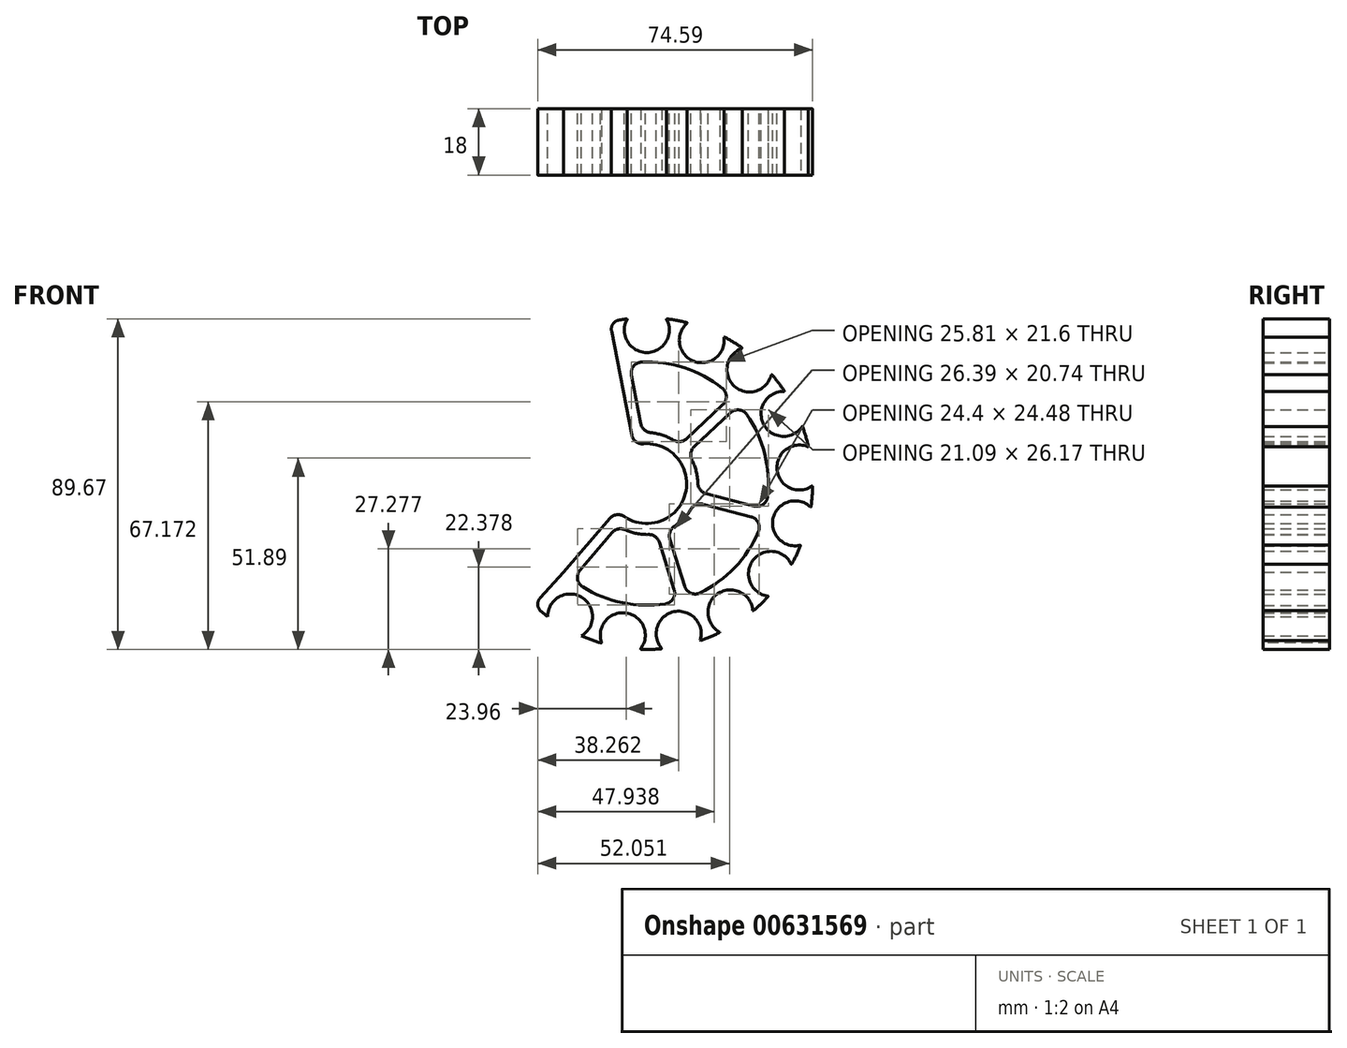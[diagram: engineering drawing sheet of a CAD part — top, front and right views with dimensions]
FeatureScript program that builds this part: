
annotation { "Feature Type Name" : "Feature", "Feature Type Description" : "" }
export const myFeature = defineFeature(function(context is Context, id is Id, definition is map)
    precondition{}
    {
        {
            var Q0;
            Q0=qCreatedBy(makeId("Front.planeOp"),FACE);
            var sketch = newSketch(context, id + "F0", { "sketchPlane" : qUnion([Q0])});
            skArc(sketch, "E0", {"start": v(-8.1, -7.18) * mm, "mid": v(10.47, -2.76) * mm, "end": v(-3.52, 10.24) * mm});
            skArc(sketch, "E1", {"start": v(-30.67, -32.93) * mm, "mid": v(43.46, -11.67) * mm, "end": v(-10.06, 43.86) * mm});
            skCircle(sketch, "E2", {"center": v(0, 41.65) * mm, "radius": 6.1 * mm});
            skCircle(sketch, "E3.1.0", {"center": v(14.93, 38.88) * mm, "radius": 6.1 * mm});
            skCircle(sketch, "E3.2.0", {"center": v(27.87, 30.95) * mm, "radius": 6.1 * mm});
            skCircle(sketch, "E3.3.0", {"center": v(37.11, 18.9) * mm, "radius": 6.1 * mm});
            skCircle(sketch, "E3.4.0", {"center": v(41.42, 4.35) * mm, "radius": 6.1 * mm});
            skCircle(sketch, "E3.5.0", {"center": v(40.23, -10.78) * mm, "radius": 6.1 * mm});
            skCircle(sketch, "E3.6.0", {"center": v(33.7, -24.48) * mm, "radius": 6.1 * mm});
            skCircle(sketch, "E3.7.0", {"center": v(22.68, -34.93) * mm, "radius": 6.1 * mm});
            skCircle(sketch, "E3.8.0", {"center": v(8.66, -40.74) * mm, "radius": 6.1 * mm});
            skCircle(sketch, "E3.9.0", {"center": v(-6.52, -41.14) * mm, "radius": 6.1 * mm});
            skLineSegment(sketch, "E3.anchor1", {"start": v(0, 0) * mm, "end": v(0, 41.65) * mm, "construction": true});
            skLineSegment(sketch, "E3.anchor2", {"start": v(0, 0) * mm, "end": v(-20.83, -36.07) * mm, "construction": true});
            skLineSegment(sketch, "E4", {"start": v(0, 0) * mm, "end": v(-8.59, 44.17) * mm, "construction": true});
            skLineSegment(sketch, "E5", {"start": v(0, 0) * mm, "end": v(-30.47, -33.11) * mm, "construction": true});
            skArc(sketch, "E6.0", {"start": v(-22.55, -24.1) * mm, "mid": v(31.91, -8.4) * mm, "end": v(-7.76, 32.07) * mm});
            skLineSegment(sketch, "E7.0", {"start": v(-0.57, 10.8) * mm, "end": v(-4.82, 32.65) * mm});
            skLineSegment(sketch, "E8.0", {"start": v(-3.52, 10.24) * mm, "end": v(-7.76, 32.07) * mm});
            skLineSegment(sketch, "E9.trimOffspring", {"start": v(-10.06, 43.86) * mm, "end": v(-10.06, 43.89) * mm});
            skLineSegment(sketch, "E10.trimOffspring", {"start": v(-7.11, 44.43) * mm, "end": v(-7.12, 44.46) * mm});
            skLineSegment(sketch, "E11.1.0", {"start": v(6.8, 8.42) * mm, "end": v(23.03, 23.63) * mm});
            skLineSegment(sketch, "E11.1.1", {"start": v(8.85, 6.23) * mm, "end": v(25.08, 21.44) * mm});
            skLineSegment(sketch, "E11.2.0", {"start": v(10.75, -1.28) * mm, "end": v(32.26, -6.94) * mm});
            skLineSegment(sketch, "E11.2.1", {"start": v(9.99, -4.18) * mm, "end": v(31.5, -9.84) * mm});
            skLineSegment(sketch, "E11.3.0", {"start": v(4.63, -9.78) * mm, "end": v(11.28, -31.01) * mm});
            skLineSegment(sketch, "E11.3.1", {"start": v(1.77, -10.68) * mm, "end": v(8.42, -31.9) * mm});
            skLineSegment(sketch, "E11.4.0", {"start": v(-5.82, -9.13) * mm, "end": v(-20.27, -26.04) * mm});
            skLineSegment(sketch, "E11.4.1", {"start": v(-8.1, -7.18) * mm, "end": v(-22.55, -24.1) * mm});
            skLineSegment(sketch, "E11.anchor1", {"start": v(0, 0) * mm, "end": v(-3.52, 10.24) * mm, "construction": true});
            skLineSegment(sketch, "E11.anchor2", {"start": v(0, 0) * mm, "end": v(-5.82, -9.13) * mm, "construction": true});
            skLineSegment(sketch, "E12", {"start": v(-10.06, 43.86) * mm, "end": v(-7.76, 32.07) * mm});
            skLineSegment(sketch, "E13", {"start": v(-22.55, -24.1) * mm, "end": v(-30.67, -32.93) * mm});
            skArc(sketch, "E14.0", {"start": v(-10.07, -9.48) * mm, "mid": v(13.37, -3.52) * mm, "end": v(-4.1, 13.2) * mm});
            skCircle(sketch, "E15.1.10.0", {"center": v(-20.83, -36.07) * mm, "radius": 6.1 * mm});
            skSolve(sketch);
        }
        {
            var Q0;
            {var subQ20=sQuery(id+"F0.wireOp",EDGE,"E0");var subQ25=sQuery(id+"F0.wireOp",EDGE,"E4");var subQ27=makeQuery(id+"F0.imprint","INTERSECT",VERTEX,{"derivedFrom":[subQ20,subQ25]});Q0=makeQuery(id+"F0.imprint","IMPRINT",FACE,{"disambiguationData":[TD([[makeQuery(id+"F0.imprint","IMPRINT",EDGE,{"disambiguationData":[TD([[subQ27,1.0]])],"derivedFrom":subQ20}),-1.0]])]});}
            var Q1;
            {var subQ1=sQuery(id+"F0.wireOp",EDGE,"E6.0");var subQ3=sQuery(id+"F0.wireOp",EDGE,"E7.0");var subQ4=makeQuery(id+"F0.imprint","INTERSECT",VERTEX,{"derivedFrom":[subQ1,subQ3]});Q1=makeQuery(id+"F0.imprint","IMPRINT",FACE,{"disambiguationData":[TD([[makeQuery(id+"F0.imprint","IMPRINT",EDGE,{"disambiguationData":[TD([[subQ4,1.0]])],"derivedFrom":subQ3}),1.0]])]});}
            var Q2;
            {var subQ0=sQuery(id+"F0.wireOp",EDGE,"E11.1.0");var subQ1=sQuery(id+"F0.wireOp",EDGE,"E6.0");var subQ2=makeQuery(id+"F0.imprint","INTERSECT",VERTEX,{"derivedFrom":[subQ1,subQ0]});Q2=makeQuery(id+"F0.imprint","IMPRINT",FACE,{"disambiguationData":[TD([[makeQuery(id+"F0.imprint","IMPRINT",EDGE,{"disambiguationData":[TD([[subQ2,1.0]])],"derivedFrom":subQ1}),1.0]])]});}
            var Q3;
            {var subQ0=sQuery(id+"F0.wireOp",EDGE,"E11.2.0");var subQ1=sQuery(id+"F0.wireOp",EDGE,"E6.0");var subQ2=makeQuery(id+"F0.imprint","INTERSECT",VERTEX,{"derivedFrom":[subQ1,subQ0]});Q3=makeQuery(id+"F0.imprint","IMPRINT",FACE,{"disambiguationData":[TD([[makeQuery(id+"F0.imprint","IMPRINT",EDGE,{"disambiguationData":[TD([[subQ2,1.0]])],"derivedFrom":subQ1}),1.0]])]});}
            var Q4;
            {var subQ0=sQuery(id+"F0.wireOp",EDGE,"E11.3.0");var subQ1=sQuery(id+"F0.wireOp",EDGE,"E6.0");var subQ2=makeQuery(id+"F0.imprint","INTERSECT",VERTEX,{"derivedFrom":[subQ1,subQ0]});Q4=makeQuery(id+"F0.imprint","IMPRINT",FACE,{"disambiguationData":[TD([[makeQuery(id+"F0.imprint","IMPRINT",EDGE,{"disambiguationData":[TD([[subQ2,1.0]])],"derivedFrom":subQ1}),1.0]])]});}
            var Q5;
            {var subQ1=sQuery(id+"F0.wireOp",EDGE,"E6.0");var subQ3=sQuery(id+"F0.wireOp",EDGE,"E11.4.0");var subQ4=makeQuery(id+"F0.imprint","INTERSECT",VERTEX,{"derivedFrom":[subQ1,subQ3]});Q5=makeQuery(id+"F0.imprint","IMPRINT",FACE,{"disambiguationData":[TD([[makeQuery(id+"F0.imprint","IMPRINT",EDGE,{"disambiguationData":[TD([[subQ4,1.0]])],"derivedFrom":subQ3}),-1.0]])]});}
            var Q6;
            {var subQ29=sQuery(id+"F0.wireOp",EDGE,"E12");Q6=makeQuery(id+"F0.imprint","IMPRINT",FACE,{"disambiguationData":[TD([[makeQuery(id+"F0.imprint","IMPRINT",EDGE,{"derivedFrom":subQ29}),1.0]])]});}
            extrude(context, id + "F1", {"entities" : qUnion([Q0, Q1, Q2, Q3, Q4, Q5, Q6]), "depth" : 18 * mm, "offsetDistance" : 25 * mm});
        }
        {
            var Q0;
            {var subQ0=sQuery(id+"F0.wireOp",EDGE,"E3.9.0");var subQ1=sQuery(id+"F0.wireOp",EDGE,"E1");Q0=makeQuery(id+"F1.opExtrude","SWEPT_EDGE",EDGE,{"disambiguationData":[OSD([subQ1,subQ0]),TDD([makeQuery(id+"F0.imprint","INTERSECT",VERTEX,{"disambiguationData":[OD(0.0)],"derivedFrom":[subQ1,subQ0]})])]});}
            var Q1;
            {var subQ0=sQuery(id+"F0.wireOp",EDGE,"E3.9.0");var subQ1=sQuery(id+"F0.wireOp",EDGE,"E1");Q1=makeQuery(id+"F1.opExtrude","SWEPT_EDGE",EDGE,{"disambiguationData":[OSD([subQ1,subQ0]),TDD([makeQuery(id+"F0.imprint","INTERSECT",VERTEX,{"disambiguationData":[OD(1.0)],"derivedFrom":[subQ1,subQ0]})])]});}
            var Q2;
            {var subQ0=sQuery(id+"F0.wireOp",EDGE,"E3.8.0");var subQ1=sQuery(id+"F0.wireOp",EDGE,"E1");Q2=makeQuery(id+"F1.opExtrude","SWEPT_EDGE",EDGE,{"disambiguationData":[OSD([subQ1,subQ0]),TDD([makeQuery(id+"F0.imprint","INTERSECT",VERTEX,{"disambiguationData":[OD(0.0)],"derivedFrom":[subQ1,subQ0]})])]});}
            var Q3;
            {var subQ0=sQuery(id+"F0.wireOp",EDGE,"E3.8.0");var subQ1=sQuery(id+"F0.wireOp",EDGE,"E1");Q3=makeQuery(id+"F1.opExtrude","SWEPT_EDGE",EDGE,{"disambiguationData":[OSD([subQ1,subQ0]),TDD([makeQuery(id+"F0.imprint","INTERSECT",VERTEX,{"disambiguationData":[OD(1.0)],"derivedFrom":[subQ1,subQ0]})])]});}
            var Q4;
            {var subQ0=sQuery(id+"F0.wireOp",EDGE,"E3.7.0");var subQ1=sQuery(id+"F0.wireOp",EDGE,"E1");Q4=makeQuery(id+"F1.opExtrude","SWEPT_EDGE",EDGE,{"disambiguationData":[OSD([subQ1,subQ0]),TDD([makeQuery(id+"F0.imprint","INTERSECT",VERTEX,{"disambiguationData":[OD(0.0)],"derivedFrom":[subQ1,subQ0]})])]});}
            var Q5;
            {var subQ0=sQuery(id+"F0.wireOp",EDGE,"E3.7.0");var subQ1=sQuery(id+"F0.wireOp",EDGE,"E1");Q5=makeQuery(id+"F1.opExtrude","SWEPT_EDGE",EDGE,{"disambiguationData":[OSD([subQ1,subQ0]),TDD([makeQuery(id+"F0.imprint","INTERSECT",VERTEX,{"disambiguationData":[OD(1.0)],"derivedFrom":[subQ1,subQ0]})])]});}
            var Q6;
            {var subQ0=sQuery(id+"F0.wireOp",EDGE,"E3.6.0");var subQ1=sQuery(id+"F0.wireOp",EDGE,"E1");Q6=makeQuery(id+"F1.opExtrude","SWEPT_EDGE",EDGE,{"disambiguationData":[OSD([subQ1,subQ0]),TDD([makeQuery(id+"F0.imprint","INTERSECT",VERTEX,{"disambiguationData":[OD(0.0)],"derivedFrom":[subQ1,subQ0]})])]});}
            var Q7;
            {var subQ0=sQuery(id+"F0.wireOp",EDGE,"E3.6.0");var subQ1=sQuery(id+"F0.wireOp",EDGE,"E1");Q7=makeQuery(id+"F1.opExtrude","SWEPT_EDGE",EDGE,{"disambiguationData":[OSD([subQ1,subQ0]),TDD([makeQuery(id+"F0.imprint","INTERSECT",VERTEX,{"disambiguationData":[OD(1.0)],"derivedFrom":[subQ1,subQ0]})])]});}
            var Q8;
            {var subQ0=sQuery(id+"F0.wireOp",EDGE,"E3.5.0");var subQ1=sQuery(id+"F0.wireOp",EDGE,"E1");Q8=makeQuery(id+"F1.opExtrude","SWEPT_EDGE",EDGE,{"disambiguationData":[OSD([subQ1,subQ0]),TDD([makeQuery(id+"F0.imprint","INTERSECT",VERTEX,{"disambiguationData":[OD(0.0)],"derivedFrom":[subQ1,subQ0]})])]});}
            var Q9;
            {var subQ0=sQuery(id+"F0.wireOp",EDGE,"E3.5.0");var subQ1=sQuery(id+"F0.wireOp",EDGE,"E1");Q9=makeQuery(id+"F1.opExtrude","SWEPT_EDGE",EDGE,{"disambiguationData":[OSD([subQ1,subQ0]),TDD([makeQuery(id+"F0.imprint","INTERSECT",VERTEX,{"disambiguationData":[OD(1.0)],"derivedFrom":[subQ1,subQ0]})])]});}
            var Q10;
            {var subQ0=sQuery(id+"F0.wireOp",EDGE,"E3.4.0");var subQ1=sQuery(id+"F0.wireOp",EDGE,"E1");Q10=makeQuery(id+"F1.opExtrude","SWEPT_EDGE",EDGE,{"disambiguationData":[OSD([subQ1,subQ0]),TDD([makeQuery(id+"F0.imprint","INTERSECT",VERTEX,{"disambiguationData":[OD(0.0)],"derivedFrom":[subQ1,subQ0]})])]});}
            var Q11;
            {var subQ0=sQuery(id+"F0.wireOp",EDGE,"E3.4.0");var subQ1=sQuery(id+"F0.wireOp",EDGE,"E1");Q11=makeQuery(id+"F1.opExtrude","SWEPT_EDGE",EDGE,{"disambiguationData":[OSD([subQ1,subQ0]),TDD([makeQuery(id+"F0.imprint","INTERSECT",VERTEX,{"disambiguationData":[OD(1.0)],"derivedFrom":[subQ1,subQ0]})])]});}
            var Q12;
            {var subQ0=sQuery(id+"F0.wireOp",EDGE,"E3.3.0");var subQ1=sQuery(id+"F0.wireOp",EDGE,"E1");Q12=makeQuery(id+"F1.opExtrude","SWEPT_EDGE",EDGE,{"disambiguationData":[OSD([subQ1,subQ0]),TDD([makeQuery(id+"F0.imprint","INTERSECT",VERTEX,{"disambiguationData":[OD(0.0)],"derivedFrom":[subQ1,subQ0]})])]});}
            var Q13;
            {var subQ0=sQuery(id+"F0.wireOp",EDGE,"E3.3.0");var subQ1=sQuery(id+"F0.wireOp",EDGE,"E1");Q13=makeQuery(id+"F1.opExtrude","SWEPT_EDGE",EDGE,{"disambiguationData":[OSD([subQ1,subQ0]),TDD([makeQuery(id+"F0.imprint","INTERSECT",VERTEX,{"disambiguationData":[OD(1.0)],"derivedFrom":[subQ1,subQ0]})])]});}
            var Q14;
            {var subQ0=sQuery(id+"F0.wireOp",EDGE,"E3.2.0");var subQ1=sQuery(id+"F0.wireOp",EDGE,"E1");Q14=makeQuery(id+"F1.opExtrude","SWEPT_EDGE",EDGE,{"disambiguationData":[OSD([subQ1,subQ0]),TDD([makeQuery(id+"F0.imprint","INTERSECT",VERTEX,{"disambiguationData":[OD(0.0)],"derivedFrom":[subQ1,subQ0]})])]});}
            var Q15;
            {var subQ0=sQuery(id+"F0.wireOp",EDGE,"E3.2.0");var subQ1=sQuery(id+"F0.wireOp",EDGE,"E1");Q15=makeQuery(id+"F1.opExtrude","SWEPT_EDGE",EDGE,{"disambiguationData":[OSD([subQ1,subQ0]),TDD([makeQuery(id+"F0.imprint","INTERSECT",VERTEX,{"disambiguationData":[OD(1.0)],"derivedFrom":[subQ1,subQ0]})])]});}
            var Q16;
            {var subQ0=sQuery(id+"F0.wireOp",EDGE,"E3.1.0");var subQ1=sQuery(id+"F0.wireOp",EDGE,"E1");Q16=makeQuery(id+"F1.opExtrude","SWEPT_EDGE",EDGE,{"disambiguationData":[OSD([subQ1,subQ0]),TDD([makeQuery(id+"F0.imprint","INTERSECT",VERTEX,{"disambiguationData":[OD(0.0)],"derivedFrom":[subQ1,subQ0]})])]});}
            var Q17;
            {var subQ0=sQuery(id+"F0.wireOp",EDGE,"E3.1.0");var subQ1=sQuery(id+"F0.wireOp",EDGE,"E1");Q17=makeQuery(id+"F1.opExtrude","SWEPT_EDGE",EDGE,{"disambiguationData":[OSD([subQ1,subQ0]),TDD([makeQuery(id+"F0.imprint","INTERSECT",VERTEX,{"disambiguationData":[OD(1.0)],"derivedFrom":[subQ1,subQ0]})])]});}
            var Q18;
            {var subQ0=sQuery(id+"F0.wireOp",EDGE,"E2");var subQ1=sQuery(id+"F0.wireOp",EDGE,"E1");Q18=makeQuery(id+"F1.opExtrude","SWEPT_EDGE",EDGE,{"disambiguationData":[OSD([subQ1,subQ0]),TDD([makeQuery(id+"F0.imprint","INTERSECT",VERTEX,{"disambiguationData":[OD(0.0)],"derivedFrom":[subQ1,subQ0]})])]});}
            var Q19;
            {var subQ0=sQuery(id+"F0.wireOp",EDGE,"E2");var subQ1=sQuery(id+"F0.wireOp",EDGE,"E1");Q19=makeQuery(id+"F1.opExtrude","SWEPT_EDGE",EDGE,{"disambiguationData":[OSD([subQ1,subQ0]),TDD([makeQuery(id+"F0.imprint","INTERSECT",VERTEX,{"disambiguationData":[OD(1.0)],"derivedFrom":[subQ1,subQ0]})])]});}
            fillet(context, id + "F2", {"entities" : qUnion([Q0, Q1, Q2, Q3, Q4, Q5, Q6, Q7, Q8, Q9, Q10, Q11, Q12, Q13, Q14, Q15, Q16, Q17, Q18, Q19]), "radius" : 0.1 * mm, "tangentPropagation" : true, "allowEdgeOverflow" : false});
        }
        {
            var Q0;
            Q0=makeQuery(id+"F1.opExtrude","SWEPT_EDGE",EDGE,{"disambiguationData":[OSD([sQuery(id+"F0.wireOp",EDGE,"E11.4.0"),sQuery(id+"F0.wireOp",EDGE,"E14.0")])]});
            var Q1;
            Q1=makeQuery(id+"F1.opExtrude","SWEPT_EDGE",EDGE,{"disambiguationData":[OSD([sQuery(id+"F0.wireOp",EDGE,"E11.3.1"),sQuery(id+"F0.wireOp",EDGE,"E14.0")])]});
            var Q2;
            Q2=makeQuery(id+"F1.opExtrude","SWEPT_EDGE",EDGE,{"disambiguationData":[OSD([sQuery(id+"F0.wireOp",EDGE,"E6.0"),sQuery(id+"F0.wireOp",EDGE,"E11.4.0")])]});
            var Q3;
            Q3=makeQuery(id+"F1.opExtrude","SWEPT_EDGE",EDGE,{"disambiguationData":[OSD([sQuery(id+"F0.wireOp",EDGE,"E6.0"),sQuery(id+"F0.wireOp",EDGE,"E11.3.1")])]});
            var Q4;
            Q4=makeQuery(id+"F1.opExtrude","SWEPT_EDGE",EDGE,{"disambiguationData":[OSD([sQuery(id+"F0.wireOp",EDGE,"E6.0"),sQuery(id+"F0.wireOp",EDGE,"E11.3.0")])]});
            var Q5;
            Q5=makeQuery(id+"F1.opExtrude","SWEPT_EDGE",EDGE,{"disambiguationData":[OSD([sQuery(id+"F0.wireOp",EDGE,"E11.3.0"),sQuery(id+"F0.wireOp",EDGE,"E14.0")])]});
            var Q6;
            Q6=makeQuery(id+"F1.opExtrude","SWEPT_EDGE",EDGE,{"disambiguationData":[OSD([sQuery(id+"F0.wireOp",EDGE,"E11.2.1"),sQuery(id+"F0.wireOp",EDGE,"E14.0")])]});
            var Q7;
            Q7=makeQuery(id+"F1.opExtrude","SWEPT_EDGE",EDGE,{"disambiguationData":[OSD([sQuery(id+"F0.wireOp",EDGE,"E6.0"),sQuery(id+"F0.wireOp",EDGE,"E11.2.1")])]});
            var Q8;
            Q8=makeQuery(id+"F1.opExtrude","SWEPT_EDGE",EDGE,{"disambiguationData":[OSD([sQuery(id+"F0.wireOp",EDGE,"E11.2.0"),sQuery(id+"F0.wireOp",EDGE,"E14.0")])]});
            var Q9;
            Q9=makeQuery(id+"F1.opExtrude","SWEPT_EDGE",EDGE,{"disambiguationData":[OSD([sQuery(id+"F0.wireOp",EDGE,"E6.0"),sQuery(id+"F0.wireOp",EDGE,"E11.2.0")])]});
            var Q10;
            Q10=makeQuery(id+"F1.opExtrude","SWEPT_EDGE",EDGE,{"disambiguationData":[OSD([sQuery(id+"F0.wireOp",EDGE,"E11.1.1"),sQuery(id+"F0.wireOp",EDGE,"E14.0")])]});
            var Q11;
            Q11=makeQuery(id+"F1.opExtrude","SWEPT_EDGE",EDGE,{"disambiguationData":[OSD([sQuery(id+"F0.wireOp",EDGE,"E6.0"),sQuery(id+"F0.wireOp",EDGE,"E11.1.1")])]});
            var Q12;
            Q12=makeQuery(id+"F1.opExtrude","SWEPT_EDGE",EDGE,{"disambiguationData":[OSD([sQuery(id+"F0.wireOp",EDGE,"E6.0"),sQuery(id+"F0.wireOp",EDGE,"E11.1.0")])]});
            var Q13;
            Q13=makeQuery(id+"F1.opExtrude","SWEPT_EDGE",EDGE,{"disambiguationData":[OSD([sQuery(id+"F0.wireOp",EDGE,"E11.1.0"),sQuery(id+"F0.wireOp",EDGE,"E14.0")])]});
            var Q14;
            Q14=makeQuery(id+"F1.opExtrude","SWEPT_EDGE",EDGE,{"disambiguationData":[OSD([sQuery(id+"F0.wireOp",EDGE,"E7.0"),sQuery(id+"F0.wireOp",EDGE,"E14.0")])]});
            var Q15;
            Q15=makeQuery(id+"F1.opExtrude","SWEPT_EDGE",EDGE,{"disambiguationData":[OSD([sQuery(id+"F0.wireOp",EDGE,"E6.0"),sQuery(id+"F0.wireOp",EDGE,"E7.0")])]});
            fillet(context, id + "F3", {"entities" : qUnion([Q0, Q1, Q2, Q3, Q4, Q5, Q6, Q7, Q8, Q9, Q10, Q11, Q12, Q13, Q14, Q15]), "radius" : 3 * mm, "tangentPropagation" : true, "allowEdgeOverflow" : false});
        }
        {
            var Q0;
            Q0=makeQuery(id+"F1.opExtrude","SWEPT_EDGE",EDGE,{"disambiguationData":[OSD([sQuery(id+"F0.wireOp",EDGE,"E0"),sQuery(id+"F0.wireOp",EDGE,"E8.0")])]});
            var Q1;
            Q1=makeQuery(id+"F1.opExtrude","SWEPT_EDGE",EDGE,{"disambiguationData":[OSD([sQuery(id+"F0.wireOp",EDGE,"E0"),sQuery(id+"F0.wireOp",EDGE,"E11.4.1")])]});
            fillet(context, id + "F4", {"entities" : qUnion([Q0, Q1]), "radius" : 3 * mm, "tangentPropagation" : true, "allowEdgeOverflow" : false});
        }
        {
            var Q0;
            Q0=makeQuery(id+"F1.opExtrude","SWEPT_EDGE",EDGE,{"disambiguationData":[OSD([sQuery(id+"F0.wireOp",EDGE,"E1"),sQuery(id+"F0.wireOp",EDGE,"E12")])]});
            var Q1;
            Q1=makeQuery(id+"F1.opExtrude","SWEPT_EDGE",EDGE,{"disambiguationData":[OSD([sQuery(id+"F0.wireOp",EDGE,"E1"),sQuery(id+"F0.wireOp",EDGE,"E13")])]});
            fillet(context, id + "F5", {"entities" : qUnion([Q0, Q1]), "radius" : 2.5 * mm, "tangentPropagation" : true, "allowEdgeOverflow" : false});
        }
    });
